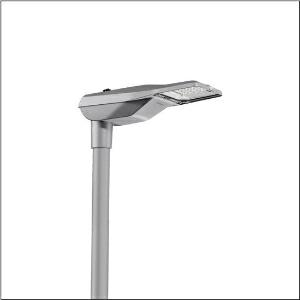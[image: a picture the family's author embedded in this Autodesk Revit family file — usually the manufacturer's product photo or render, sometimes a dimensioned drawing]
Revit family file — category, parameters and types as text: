
# Revit family: streetlight_sl_21_iq_micro___st1_0a_5xe1d31v08db_4967
name_source: partatom
category: Lighting Fixtures
units: mm (PartAtom-declared; Revit-internal decimal feet)

## family parameters
Cut with Voids When Loaded = No
Host = Face
Light Source = No
Part Type = Normal
Room Calculation Point = No
Round Connector Dimension = Use Diameter
Shared = No

## types (1)
- --- (1 x LED, 5110 lm, 39.1 W, 3000K)
    Apparent Load = 39 VA
    CIE Flux Codes = 37 72 97 100 100
    Color Rendering = 70
    Color Temperature = 3000K
    Default Elevation = 1800 mm
    Description = Streetlight SL 21 iQ micro, mast luminaire, primary light control with lens, of PMMA, primary optical cover: cover, of toughened safety glass, transparent, light distribution: ST1.0a, light emission: direct distribution, primary light characteristic: asymmetric, installation type: post-top, side-entry, LED, High Power LED, rated luminous flux: 5.110lm, luminous efficacy: 131lm/W, light colour: 730, colour temperature: 3000K, control: pre-setting: logarithmic dimming characteristic, Street-Remote, Auto-Match, Temp-Guard, Lumen-Switch, Night-Set, Smart-Wire, Light-Fading, Desk-Remote (wireless, voltage-free reading and setting of iQ features in the workshop via application-optimized NFC function/RFID function), optimised constant luminous flux control (CLO 2.0), mains connection: 220..240V, AC, 50/60Hz, start of lifetime: 39W, end of service life: 41W, reduction: 17W, luminaire housing, of diecast aluminium, powder-coated, Siteco® metallic grey (DB 702S), corrosivity category C5 mid according to DIN EN ISO 12944, please order mast flange separately, inclination adjustable: 0°, 5°, 10°, 15°, sealing non-destructively replaceable, multi-level sealing system, length: 528mm, width: 235mm, height: 110mm, mast flange for spigot size: 42mm (side-entry): 5XC10008XM4, 60/48mm (side-entry/post-top): 5XC10108XM2, 76/60mm (side-entry/post-top): 5XC10108XM1, Smart Interface above, protection rating (complete): IP66, insulation class (complete): insulation class II (safety insulation), certification: CE, ENEC, ENEC+, VDE, impact resistance: IK09, permissible operating ambient temperature for outdoor applications: -40..+50°C, standard-compliant lighting for roads and squares, packaging unit: 1 piece

Light Distribution: ST1.0a
    Height = 110 mm
    Lamp = 1 x LED
    Lamp Light Flux = 5110 lm
    Lamp Power = 39.1 W
    Lamp count = 1
    Length = 528 mm
    Luminous efficacy = 131 lm/W
    Manufacturer = Siteco
    ModVariant = No
    Model = 5XE1D31V08DB
    Number of Poles = 1
    OnlyDefault = Yes
    Power Factor = 1
    Product Name = Streetlight SL 21 iQ micro | ST1.0a
    Product group = mast luminaire | pylon top
    ProductGroupID = 6100
    Protection Class = Protection class II
    Protection Degree = IP 66
    RLX_Detail_Level = 1
    RLX_Emergency_Light_Flux = 0 lm
    RLX_Emergency_Type = 0
    RLX_Emergency_Type_DB = No
    RlxData = <blob elided: 98517 chars, md5=859128dc>
    Socket = socket
    Standby Power = 0 W
    System Light Flux = 5110 lm
    System Power = 39 W
    Type Comments = factory setting: luminous flux: 100 % | dim-lin: 254 | 765 mA
    Type Image = l_1277292.jpg
    URL = http://relux.com
    VarID = @adj_084493
    Voltage = 0 V
    Weight = 0.00 kg
    Width = 235 mm

## geometry (parser evidence)
native form markers: Blend x4, Sweep x11
no freeform markers — native parametric forms only
